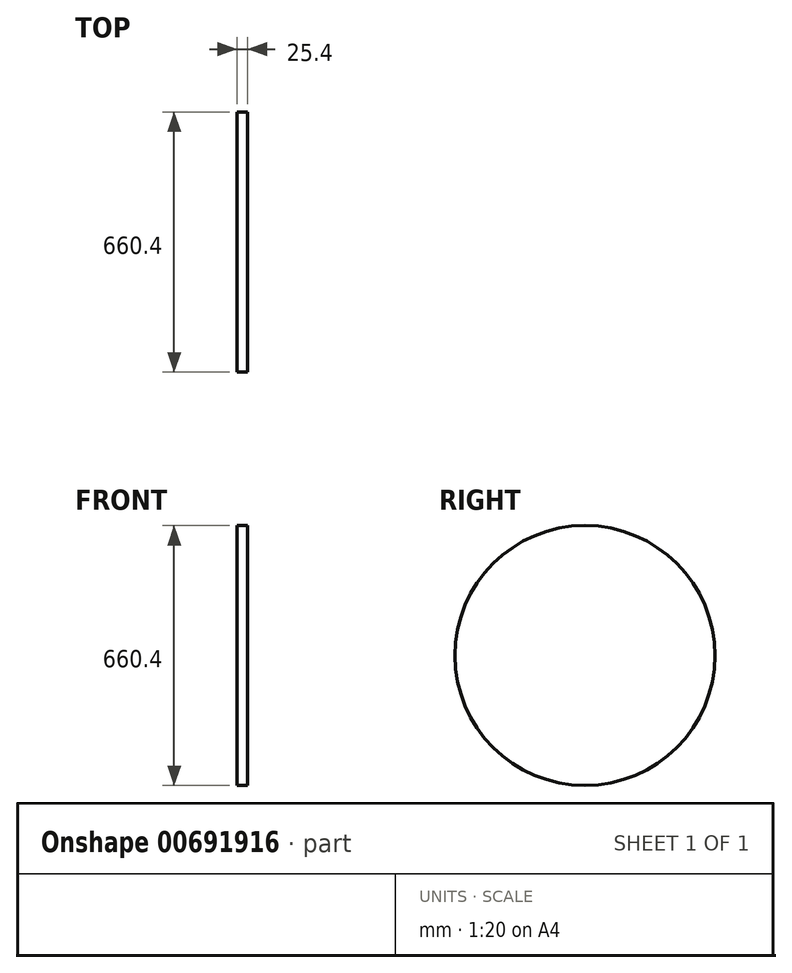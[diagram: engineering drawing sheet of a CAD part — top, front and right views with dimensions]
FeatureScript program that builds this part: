
annotation { "Feature Type Name" : "Feature", "Feature Type Description" : "" }
export const myFeature = defineFeature(function(context is Context, id is Id, definition is map)
    precondition{}
    {
        {
            var Q0;
            Q0=qCreatedBy(makeId("Right.planeOp"),FACE);
            var sketch = newSketch(context, id + "F0", { "sketchPlane" : qUnion([Q0])});
            skCircle(sketch, "E0", {"center": v(0, 0) * mm, "radius": 330.2 * mm});
            skSolve(sketch);
        }
        {
            var Q0;
            Q0=qSketchRegion(id+"F0",true);
            extrude(context, id + "F1", {"entities" : qUnion([Q0]), "endBound" : BoundingType.SYMMETRIC, "depth" : 25.4 * mm, "offsetDistance" : 25.4 * mm});
        }
    });
